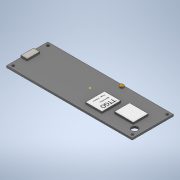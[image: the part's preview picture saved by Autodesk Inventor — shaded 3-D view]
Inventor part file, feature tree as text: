
AUTODESK INVENTOR PART (.ipt)
format: ipt  version: 2020 (Build 240168000, 168)  size: 180,224 bytes
history: native  units: mm
features: sketch x8, extrude x5, other x2
ambient origin geometry x8: Origin, YZ Plane, XZ Plane, XY Plane, X Axis, Y Axis, Z Axis, Center Point
bodies: Body1 (feature_tree)
feature tree (15):
  other  "Sólido1"
  extrude  "Extrusión1"  Depth=50.065mm
  extrude  "Extrusión2"  Depth=2.0mm
  extrude  "Extrusión3"  Depth=2.0mm
  sketch  "Boceto4"  dims[d11=2.67mm d12=2.67mm]
  sketch  "Boceto5"  dims[d13=2.0mm d14=2.0mm]
  sketch  "Boceto6"  dims[d15=2.59mm]
  extrude  "Extrusión4"  Depth=2.67mm
  extrude  "Extrusión5"  Depth=2.0mm
  other  "antena"
  sketch  "Boceto1"  dims[d3=16.445mm d4=50.065mm]
  sketch  "Boceto2"  dims[d5=1.4mm d6=0.0mm d7=2.0mm]
  sketch  "Boceto3"  dims[d8=2.0mm d10=2.59mm]
  sketch  "Boceto7"  dims[d16=2.59mm]
  sketch  "Boceto8"  dims[d17=2.36mm d18=2.36mm d19=1.4mm d20=0.0mm d22=10.0mm d23=5.0mm d24=13.0mm d25=15.0mm d26=42.0mm d27=28.0mm d28=15.0mm d29=12.0mm d30=24.0mm d31=23.0mm d32=1.4mm d33=0.0mm d34=5.0mm d38=3.0mm d39=5.0mm d40=1.4mm d41=0.0mm d42=3.0mm d43=41.0mm d44=1.0mm d45=0.0mm]
